# Revit family: 2CKA001032A0508
name_source: partatom
category: Elektroinstallationen
revit_build: Autodesk Revit 2017 (Build: 20160225_1515(x64)
units: mm (PartAtom-declared; Revit-internal decimal feet)

## family parameters
Basisbauteil = Fläche
Beim Laden mit Abzugskörper schneiden = Nein
Bemaßung runder Anschluss = Durchmesser verwenden
Beschriftungsausrichtung beibehalten = Nein
Gemeinsam genutzt = Nein
Raumberechnungspunkt = Nein
Teiletyp = Normal

## types (1)
- 2CKA001032A0508
    BIM = https://media.live.bim.site
    BIMSITE_PRODUCT_ID = d4d4867d882687865c5d3d82a32c0320257a7c1a
    Befestigungsart = Krallen-/Schraubbefestigung
    Beschreibung = El. Raumtemperaturregler UP, UP-Montagedosen und -Einsätze, Einsätze für Raumtemperaturregler, El. Raumtemperaturregler UP Wechsler, Sollwert-Anzeige, Timer Mit Wechselkontakt und thermischer Rückführung. Einfache Einstellung über menu- und textgeführte Anzeige. 4 Schaltzeiten pro Tag für jeden Wochentag frei einstellbar. Mit Spreizbefestigung Automatische Sommer-/Winterzeit-Zeitumschaltung Gangreserve > 10 Stunden. Passend für Zentralscheibe 6435-xxx. Klasse des Temperaturreglers: 1 Beitrag zur Raumheizungsenergieeffizienz: 1,0%. Nennstrom: 10 A Temperaturbereich Gerät: 5 °C bis 30 °C EN 60730-2-9
    Datenblatt = https://media.live.bim.site
    Datenblatt 1 = https://media.live.bim.site
    Datenblatt 2 = https://media.live.bim.site
    Datenblatt 3 = https://media.live.bim.site
    Datenblatt 4 = https://media.live.bim.site U-101_CE_XX_V01_2CKA100000E0134.pdf
    Datenblatt 5 = https://media.live.bim.site
    GTIN = 4011395146644
    Glass = Glass
    HAN = 2CKA001032A0508
    Halogenfrei = Ja
    HeinzeBIM = https://www.heinze.de
    Hersteller = Busch-Jaeger Elektro GmbH
    Ist System = Nein
    Ist Zubehör = Nein
    Montageart = unter Putz
    Produktseite = https://media.live.bim.site
    TYPE = 1098 U-101
    Typname = El. Raumtemperaturregler UP, UP-Montagedosen und -Einsätze, Einsätze für Raumtemperaturregler
    Vorgabe-Ansicht = 1219 mm
    White = White

## geometry (parser evidence)
native form markers: Sweep x3
no freeform markers — native parametric forms only
